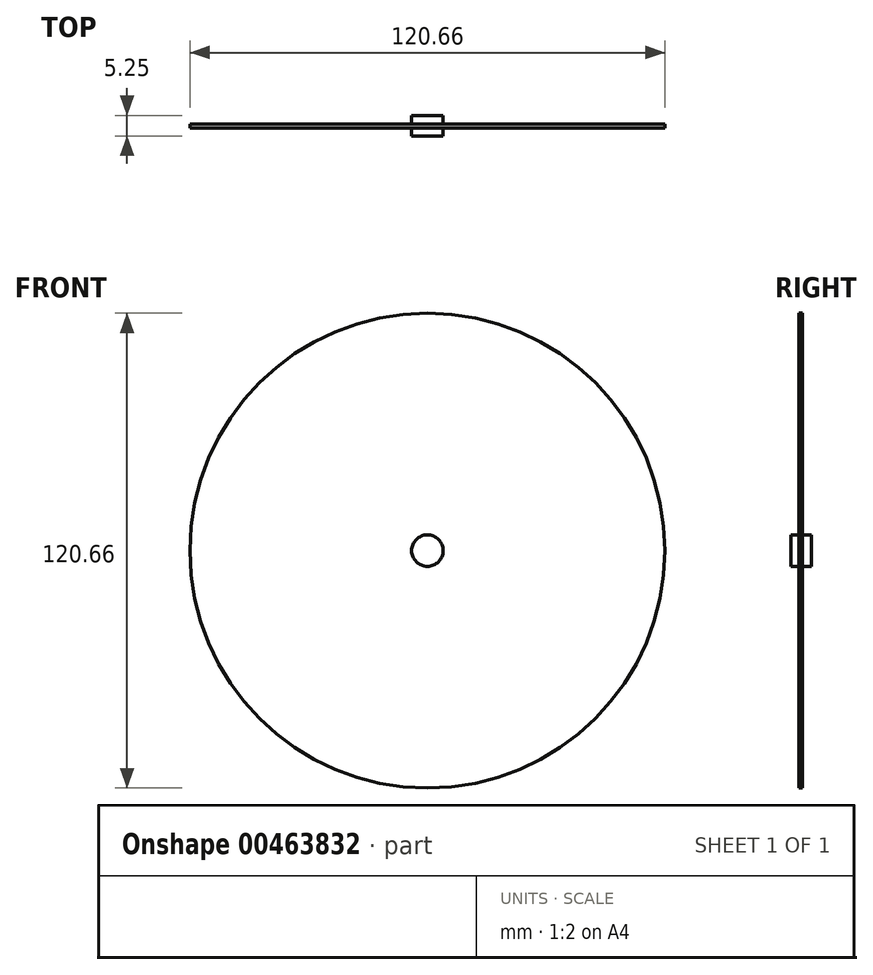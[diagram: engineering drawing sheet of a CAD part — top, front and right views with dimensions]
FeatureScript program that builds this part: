
annotation { "Feature Type Name" : "Feature", "Feature Type Description" : "" }
export const myFeature = defineFeature(function(context is Context, id is Id, definition is map)
    precondition{}
    {
        {
            var Q0;
            Q0=qCreatedBy(makeId("Front.planeOp"),FACE);
            var sketch = newSketch(context, id + "F0", { "sketchPlane" : qUnion([Q0])});
            skCircle(sketch, "E0", {"center": v(0, 0) * mm, "radius": 60.33 * mm});
            skSolve(sketch);
        }
        {
            var Q0;
            Q0=makeQuery(id+"F0.imprint","IMPRINT",FACE,{"disambiguationData":[TD([[makeQuery(id+"F0.imprint","IMPRINT",EDGE,{"derivedFrom":sQuery(id+"F0.wireOp",EDGE,"E0")}),1.0]])]});
            var sketch = newSketch(context, id + "F1", { "sketchPlane" : qUnion([Q0])});
            skCircle(sketch, "E1", {"center": v(0, 0) * mm, "radius": 4 * mm});
            skSolve(sketch);
        }
        {
            var Q0;
            Q0=makeQuery(id+"F1.imprint","IMPRINT",FACE,{"disambiguationData":[TD([[makeQuery(id+"F1.imprint","IMPRINT",EDGE,{"derivedFrom":sQuery(id+"F1.wireOp",EDGE,"E1")}),1.0]])]});
            extrude(context, id + "F2", {"entities" : qUnion([Q0]), "depth" : 3 * mm});
        }
        {
            var Q0;
            Q0=makeQuery(id+"F0.imprint","IMPRINT",FACE,{"disambiguationData":[TD([[makeQuery(id+"F0.imprint","IMPRINT",EDGE,{"derivedFrom":sQuery(id+"F0.wireOp",EDGE,"E0")}),1.0]])]});
            extrude(context, id + "F3", {"entities" : qUnion([Q0]), "operationType" : NewBodyOperationType.ADD, "depth" : 1 * mm});
        }
        {
            var Q0;
            Q0=makeQuery(id+"F3.boolean.opBoolean","MERGE",FACE,{"derivedFrom":[makeQuery(id+"F2.opExtrude","CAP_FACE",FACE,{"disambiguationData":[OSD([sQuery(id+"F1.wireOp",EDGE,"E1")])],"isStart":true}),makeQuery(id+"F3.opExtrude","CAP_FACE",FACE,{"disambiguationData":[OSD([sQuery(id+"F0.wireOp",EDGE,"E0")])],"isStart":true})]});
            var sketch = newSketch(context, id + "F4", { "sketchPlane" : qUnion([Q0])});
            skCircle(sketch, "E2", {"center": v(0, 0) * mm, "radius": 4 * mm});
            skSolve(sketch);
        }
        {
            var Q0;
            Q0=makeQuery(id+"F4.imprint","IMPRINT",FACE,{"disambiguationData":[TD([[makeQuery(id+"F4.imprint","IMPRINT",EDGE,{"derivedFrom":sQuery(id+"F4.wireOp",EDGE,"E2")}),1.0]])]});
            extrude(context, id + "F5", {"entities" : qUnion([Q0]), "operationType" : NewBodyOperationType.ADD, "depth" : 2.25 * mm});
        }
    });
